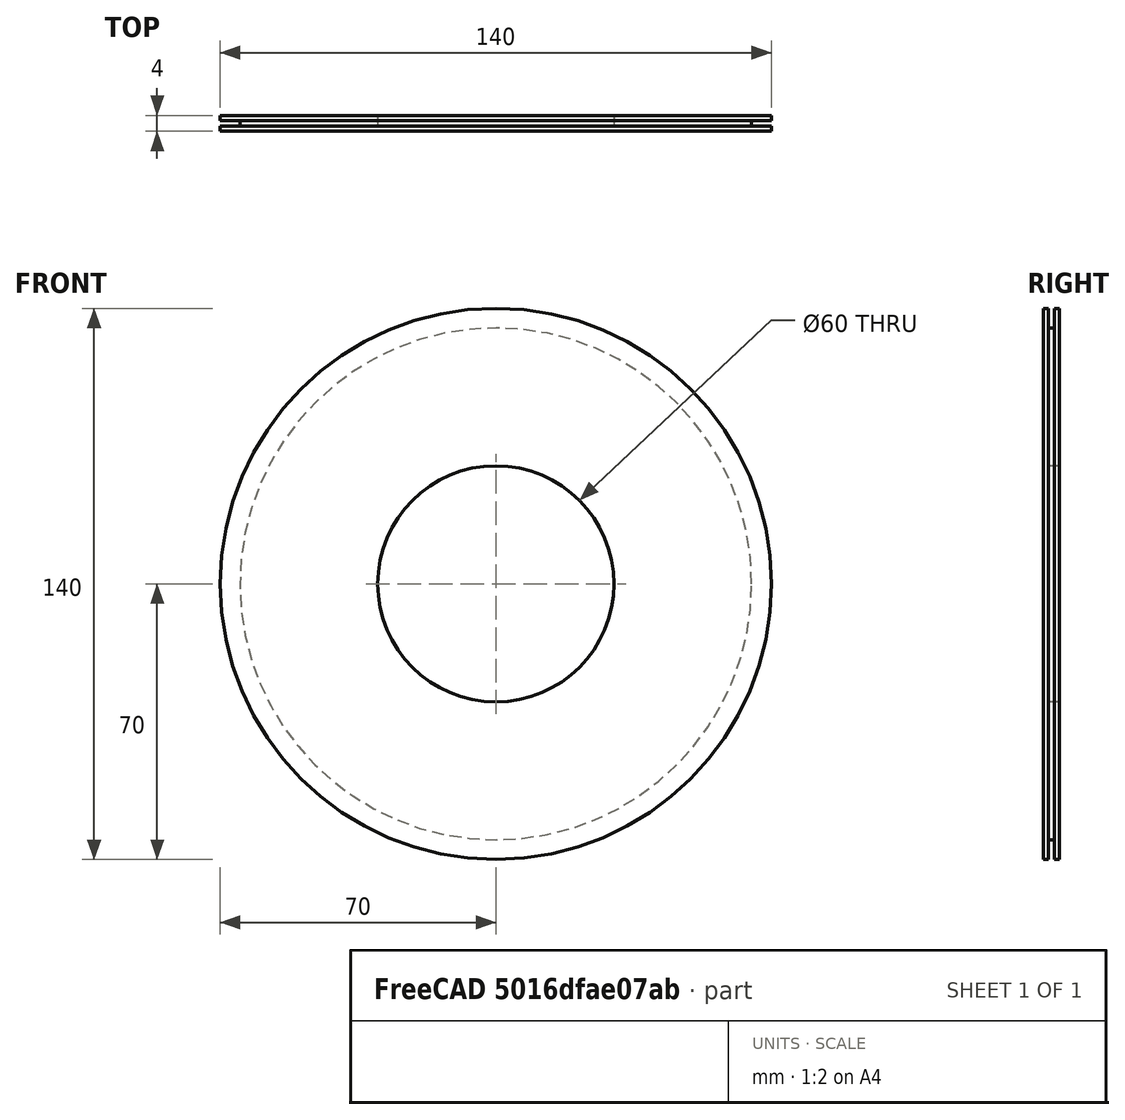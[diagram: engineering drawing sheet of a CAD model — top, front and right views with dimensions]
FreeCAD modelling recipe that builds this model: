
FCSTD DOCUMENT
Label: hautbase
objects: Sketcher::SketchObject×1, PartDesign::Revolution×1
note: 3 computed .brp shape members not serialized (recipe doc carries the construction recipe); baked Part::Feature solids carry a one-line shape summary decoded from their .brp

FEATURE [Sketcher::SketchObject] Sketch
  sketch-geometry (8):
    g0: LineSegment StartX=70 StartY=0 StartZ=0 EndX=70 EndY=1.25 EndZ=0
    g1: LineSegment StartX=70 StartY=1.25 StartZ=0 EndX=65 EndY=1.25 EndZ=0
    g2: LineSegment StartX=65 StartY=1.25 StartZ=0 EndX=65 EndY=2.75 EndZ=0
    g3: LineSegment StartX=65 StartY=2.75 StartZ=0 EndX=70 EndY=2.75 EndZ=0
    g4: LineSegment StartX=70 StartY=2.75 StartZ=0 EndX=70 EndY=4 EndZ=0
    g5: LineSegment StartX=70 StartY=4 StartZ=0 EndX=30 EndY=4 EndZ=0
    g6: LineSegment StartX=70 StartY=0 StartZ=0 EndX=30 EndY=0 EndZ=0
    g7: LineSegment StartX=30 StartY=4 StartZ=0 EndX=30 EndY=0 EndZ=0
  constraints (25):
    c: Vertical(g0)
    c: Coincident(g1,g0)
    c: Vertical(g2)
    c: Coincident(g3,g2)
    c: Vertical(g4)
    c: Distance(g0) = 1.25
    c: Parallel(g1,g3)
    c: Coincident(g1,g2)
    c: Coincident(g4,g3)
    c: Distance(g2) = 1.5
    c: Distance(g1) = 5
    c: Coincident(g5,g4)
    c: Horizontal(g5)
    c: Coincident(g6,g0)
    c: Horizontal(g6)
    c: Distance(g5) = 40
    c: Distance(g3) = 5
    c: Distance(g6) = 40
    c: Vertical(g7)
    c: Coincident(g6,g7)
    c: DistanceX(g-1,g6) = 30
    c: Distance(g4) = 1.25
    c: Parallel(g1,g6)
    c: Coincident(g7,g5)
    c: DistanceY(g-1,g6) = 0
FEATURE [PartDesign::Revolution] Revolution
  Angle = 360
  Axis = (0,1,0)
  Base = (0,0,0)
  ReferenceAxis = -> Sketch [V_Axis]
  Sketch = -> Sketch
